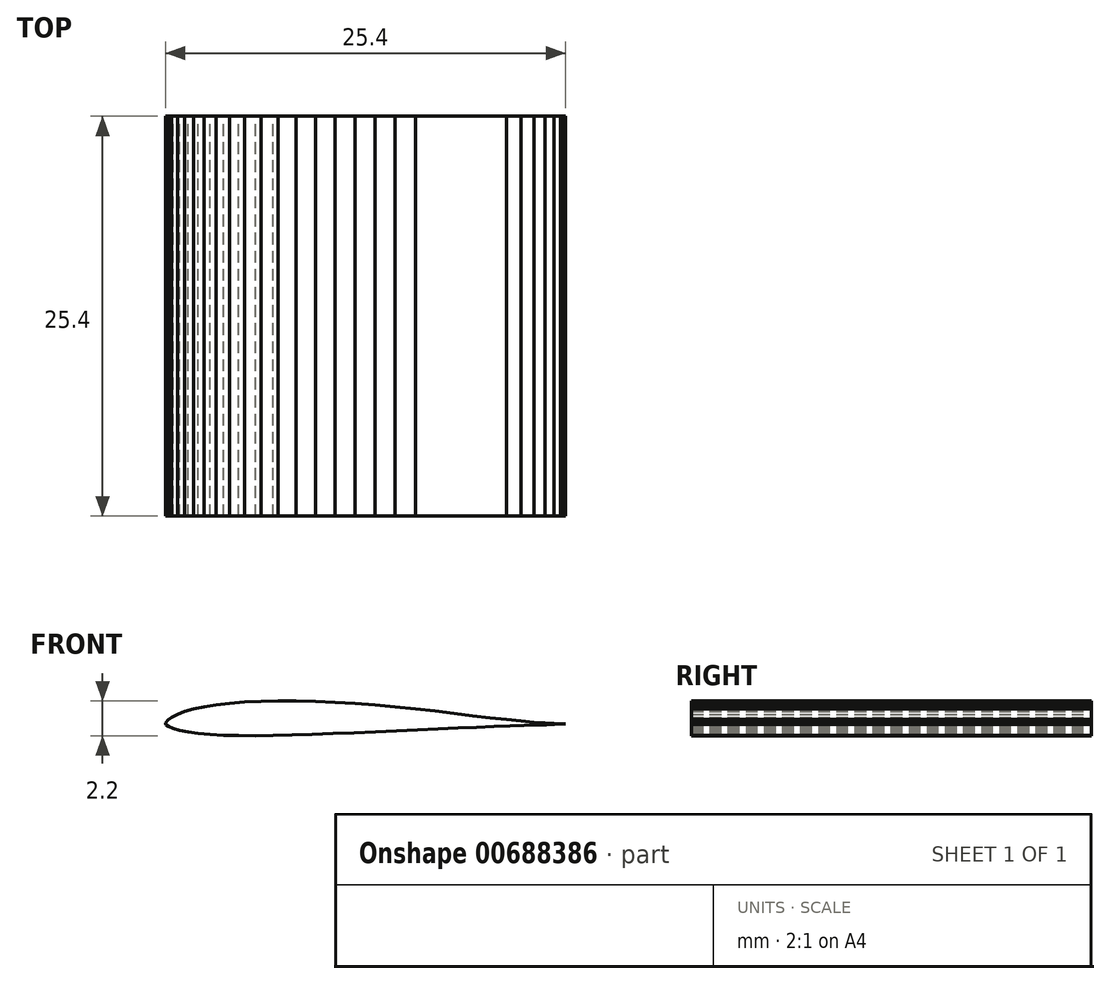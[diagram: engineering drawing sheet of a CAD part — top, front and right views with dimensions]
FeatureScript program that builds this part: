
annotation { "Feature Type Name" : "Feature", "Feature Type Description" : "" }
export const myFeature = defineFeature(function(context is Context, id is Id, definition is map)
    precondition{}
    {
        {
            var Q0;
            Q0=qCreatedBy(makeId("Front.planeOp"),FACE);
            var sketch = newSketch(context, id + "F0", { "sketchPlane" : qUnion([Q0])});
            skLineSegment(sketch, "E0", {"start": v(12.7, -0.34) * mm, "end": v(12.62, -0.34) * mm});
            skLineSegment(sketch, "E1", {"start": v(12.62, -0.34) * mm, "end": v(12.37, -0.34) * mm});
            skLineSegment(sketch, "E2", {"start": v(12.37, -0.34) * mm, "end": v(11.97, -0.32) * mm});
            skLineSegment(sketch, "E3", {"start": v(11.97, -0.32) * mm, "end": v(11.4, -0.3) * mm});
            skLineSegment(sketch, "E4", {"start": v(11.4, -0.3) * mm, "end": v(10.71, -0.25) * mm});
            skLineSegment(sketch, "E5", {"start": v(10.71, -0.25) * mm, "end": v(9.88, -0.17) * mm});
            skLineSegment(sketch, "E6", {"start": v(9.88, -0.17) * mm, "end": v(8.95, -0.08) * mm});
            skLineSegment(sketch, "E7", {"start": v(8.95, -0.08) * mm, "end": v(7.91, 0.04) * mm});
            skLineSegment(sketch, "E8", {"start": v(7.91, 0.04) * mm, "end": v(6.8, 0.17) * mm});
            skLineSegment(sketch, "E9", {"start": v(6.8, 0.17) * mm, "end": v(5.63, 0.32) * mm});
            skLineSegment(sketch, "E10", {"start": v(5.63, 0.32) * mm, "end": v(4.41, 0.46) * mm});
            skLineSegment(sketch, "E11", {"start": v(4.41, 0.46) * mm, "end": v(3.16, 0.6) * mm});
            skLineSegment(sketch, "E12", {"start": v(3.16, 0.6) * mm, "end": v(1.89, 0.73) * mm});
            skLineSegment(sketch, "E13", {"start": v(1.89, 0.73) * mm, "end": v(0.6, 0.85) * mm});
            skLineSegment(sketch, "E14", {"start": v(0.6, 0.85) * mm, "end": v(-0.68, 0.94) * mm});
            skLineSegment(sketch, "E15", {"start": v(-0.68, 0.94) * mm, "end": v(-1.95, 1.01) * mm});
            skLineSegment(sketch, "E16", {"start": v(-1.95, 1.01) * mm, "end": v(-3.2, 1.07) * mm});
            skLineSegment(sketch, "E17", {"start": v(-3.2, 1.07) * mm, "end": v(-4.4, 1.1) * mm});
            skLineSegment(sketch, "E18", {"start": v(-4.4, 1.1) * mm, "end": v(-5.55, 1.1) * mm});
            skLineSegment(sketch, "E19", {"start": v(-5.55, 1.1) * mm, "end": v(-6.65, 1.08) * mm});
            skLineSegment(sketch, "E20", {"start": v(-6.65, 1.08) * mm, "end": v(-7.68, 1.03) * mm});
            skLineSegment(sketch, "E21", {"start": v(-7.68, 1.03) * mm, "end": v(-8.63, 0.96) * mm});
            skLineSegment(sketch, "E22", {"start": v(-8.63, 0.96) * mm, "end": v(-9.49, 0.86) * mm});
            skLineSegment(sketch, "E23", {"start": v(-9.49, 0.86) * mm, "end": v(-10.25, 0.73) * mm});
            skLineSegment(sketch, "E24", {"start": v(-10.25, 0.73) * mm, "end": v(-10.92, 0.6) * mm});
            skLineSegment(sketch, "E25", {"start": v(-10.92, 0.6) * mm, "end": v(-11.5, 0.43) * mm});
            skLineSegment(sketch, "E26", {"start": v(-11.5, 0.43) * mm, "end": v(-11.95, 0.25) * mm});
            skLineSegment(sketch, "E27", {"start": v(-11.95, 0.25) * mm, "end": v(-12.3, 0.07) * mm});
            skLineSegment(sketch, "E28", {"start": v(-12.3, 0.07) * mm, "end": v(-12.55, -0.11) * mm});
            skLineSegment(sketch, "E29", {"start": v(-12.55, -0.11) * mm, "end": v(-12.69, -0.27) * mm});
            skLineSegment(sketch, "E30", {"start": v(-12.69, -0.27) * mm, "end": v(-12.7, -0.34) * mm});
            skLineSegment(sketch, "E31", {"start": v(-12.7, -0.34) * mm, "end": v(-12.68, -0.4) * mm});
            skLineSegment(sketch, "E32", {"start": v(-12.68, -0.4) * mm, "end": v(-12.52, -0.52) * mm});
            skLineSegment(sketch, "E33", {"start": v(-12.52, -0.52) * mm, "end": v(-12.24, -0.65) * mm});
            skLineSegment(sketch, "E34", {"start": v(-12.24, -0.65) * mm, "end": v(-11.82, -0.76) * mm});
            skLineSegment(sketch, "E35", {"start": v(-11.82, -0.76) * mm, "end": v(-11.29, -0.86) * mm});
            skLineSegment(sketch, "E36", {"start": v(-11.29, -0.86) * mm, "end": v(-10.64, -0.95) * mm});
            skLineSegment(sketch, "E37", {"start": v(-10.64, -0.95) * mm, "end": v(-9.88, -1.02) * mm});
            skLineSegment(sketch, "E38", {"start": v(-9.88, -1.02) * mm, "end": v(-9.02, -1.07) * mm});
            skLineSegment(sketch, "E39", {"start": v(-9.02, -1.07) * mm, "end": v(-8.05, -1.1) * mm});
            skLineSegment(sketch, "E40", {"start": v(-8.05, -1.1) * mm, "end": v(-7, -1.1) * mm});
            skLineSegment(sketch, "E41", {"start": v(-7, -1.1) * mm, "end": v(-5.86, -1.09) * mm});
            skLineSegment(sketch, "E42", {"start": v(-5.86, -1.09) * mm, "end": v(-4.65, -1.06) * mm});
            skLineSegment(sketch, "E43", {"start": v(-4.65, -1.06) * mm, "end": v(-3.39, -1.02) * mm});
            skLineSegment(sketch, "E44", {"start": v(-3.39, -1.02) * mm, "end": v(-2.08, -0.97) * mm});
            skLineSegment(sketch, "E45", {"start": v(-2.08, -0.97) * mm, "end": v(-0.73, -0.91) * mm});
            skLineSegment(sketch, "E46", {"start": v(-0.73, -0.91) * mm, "end": v(0.62, -0.85) * mm});
            skLineSegment(sketch, "E47", {"start": v(0.62, -0.85) * mm, "end": v(1.98, -0.8) * mm});
            skLineSegment(sketch, "E48", {"start": v(1.98, -0.8) * mm, "end": v(3.31, -0.73) * mm});
            skLineSegment(sketch, "E49", {"start": v(3.31, -0.73) * mm, "end": v(4.61, -0.67) * mm});
            skLineSegment(sketch, "E50", {"start": v(4.61, -0.67) * mm, "end": v(5.86, -0.62) * mm});
            skLineSegment(sketch, "E51", {"start": v(5.86, -0.62) * mm, "end": v(7.05, -0.57) * mm});
            skLineSegment(sketch, "E52", {"start": v(7.05, -0.57) * mm, "end": v(8.15, -0.52) * mm});
            skLineSegment(sketch, "E53", {"start": v(8.15, -0.52) * mm, "end": v(9.16, -0.49) * mm});
            skLineSegment(sketch, "E54", {"start": v(9.16, -0.49) * mm, "end": v(10.06, -0.45) * mm});
            skLineSegment(sketch, "E55", {"start": v(10.06, -0.45) * mm, "end": v(10.84, -0.42) * mm});
            skLineSegment(sketch, "E56", {"start": v(10.84, -0.42) * mm, "end": v(11.5, -0.4) * mm});
            skLineSegment(sketch, "E57", {"start": v(11.5, -0.4) * mm, "end": v(12.01, -0.38) * mm});
            skLineSegment(sketch, "E58", {"start": v(12.01, -0.38) * mm, "end": v(12.39, -0.36) * mm});
            skLineSegment(sketch, "E59", {"start": v(12.39, -0.36) * mm, "end": v(12.62, -0.35) * mm});
            skLineSegment(sketch, "E60", {"start": v(12.62, -0.35) * mm, "end": v(12.7, -0.34) * mm});
            skSolve(sketch);
        }
        {
            var Q0;
            Q0=makeQuery(id+"F0.imprint","IMPRINT",FACE,{"disambiguationData":[TD([[makeQuery(id+"F0.imprint","IMPRINT",EDGE,{"derivedFrom":sQuery(id+"F0.wireOp",EDGE,"E0")}),1.0]])]});
            extrude(context, id + "F1", {"entities" : qUnion([Q0]), "depth" : 25.4 * mm, "offsetDistance" : 25.4 * mm});
        }
    });
